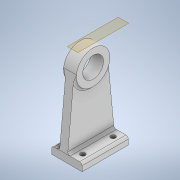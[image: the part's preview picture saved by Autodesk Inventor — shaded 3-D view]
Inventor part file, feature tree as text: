
AUTODESK INVENTOR PART (.ipt)
format: ipt  version: 2021 (Build 250183000, 183)  size: 179,712 bytes
history: native  units: mm
features: extrude x6, fillet x6, sketch x2, plane x1
ambient origin geometry x8: Origin, YZ Plane, XZ Plane, XY Plane, X Axis, Y Axis, Z Axis, Center Point
bodies: Solid1 (feature_tree)
feature tree (15):
  sketch  "Sketch1"  dims[d0=58.0mm d1=29.0mm]
  extrude  "Extrusion1"  Depth=29.0mm
  extrude  "Extrusion2"  Depth=3.0mm
  extrude  "Extrusion3"  Depth=3.0mm
  extrude  "Extrusion4"  Depth=3.0mm
  extrude  "Extrusion5"  Depth=3.0mm TaperAngle=0.0deg
  fillet  "Fillet1"  Radius=10.0mm
  fillet  "Fillet2"  Radius=10.0mm
  fillet  "Fillet3"  Radius=13.0mm
  fillet  "Fillet4"  Radius=3.0mm
  fillet  "Fillet5"  Radius=3.0mm
  plane  "Work Plane1"
  extrude  "Extrusion6"  Depth=3.0mm
  fillet  "Fillet6"  Radius=3.0mm
  sketch  "Sketch2"  dims[d2=9.5mm d3=26.0mm d4=42.0mm d5=82.0mm d6=28.0mm d7=0.0mm d8=10.0mm d9=0.0mm d10=10.0mm d11=0.0mm d12=13.0mm d13=0.0mm d14=3.0mm d15=0.0mm d16=3.0mm d17=3.0mm d18=3.0mm d19=3.0mm d20=3.0mm d21=120.0mm d22=10.0mm d23=6.0mm d24=9.0mm d25=6.0mm d26=9.0mm d27=10.0mm d28=0.0mm d29=0.0mm d30=3.0mm]
